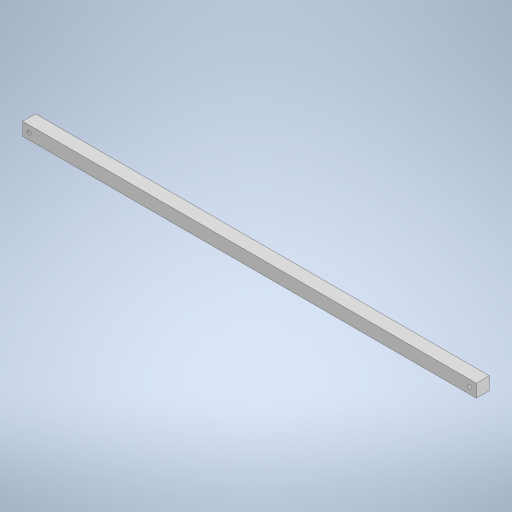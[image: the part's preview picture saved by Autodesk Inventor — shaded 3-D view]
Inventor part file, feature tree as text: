
AUTODESK INVENTOR PART (.ipt)
format: ipt  version: 2023 (Build 270158000, 158)  size: 243,200 bytes
history: native  units: mm
features: sketch x2, other x1, extrude x1, hole x1
ambient origin geometry x8: Origin, YZ Plane, XZ Plane, XY Plane, X Axis, Y Axis, Z Axis, Center Point
bodies: Body1 (feature_tree)
feature tree (5):
  other  "ソリッド1"
  extrude  "押し出し1"  Depth=350.0mm
  hole  "穴1"  [1 undecoded]
  sketch  "スケッチ1"
  sketch  "スケッチ2"
note: 1 required parameter value undecoded (feature->parameter linkage not recoverable at this tier; creation-order binding heuristic only, values carry confidence <= 0.55)
